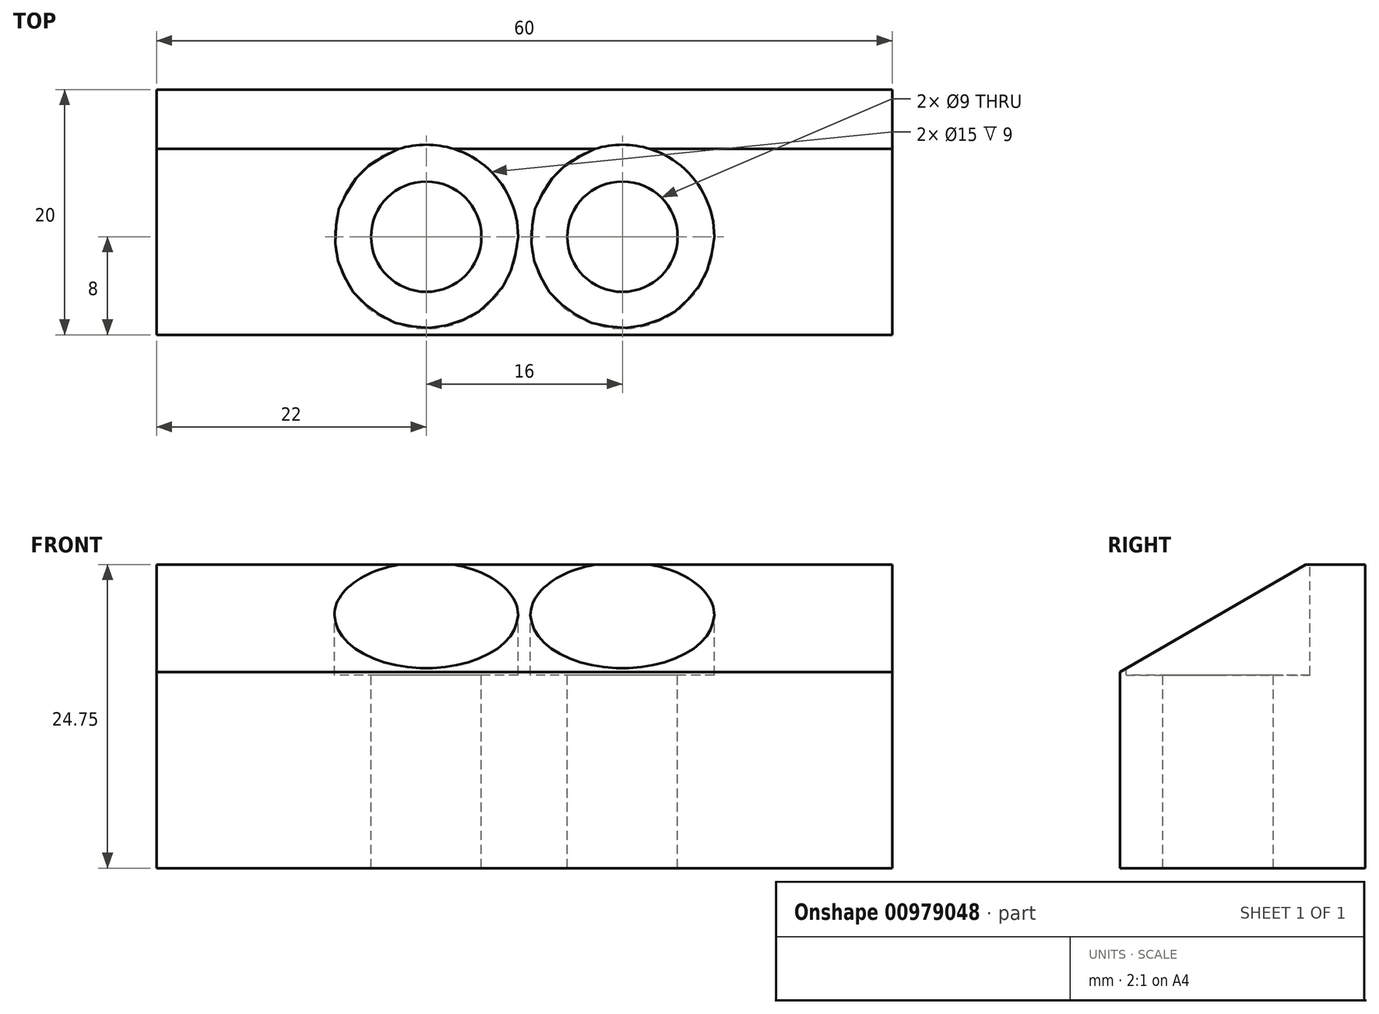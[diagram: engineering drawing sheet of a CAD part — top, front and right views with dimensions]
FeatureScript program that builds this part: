
annotation { "Feature Type Name" : "Feature", "Feature Type Description" : "" }
export const myFeature = defineFeature(function(context is Context, id is Id, definition is map)
    precondition{}
    {
        {
            var Q0;
            Q0=qCreatedBy(makeId("Right.planeOp"),FACE);
            var sketch = newSketch(context, id + "F0", { "sketchPlane" : qUnion([Q0])});
            skLineSegment(sketch, "E0", {"start": v(0, 0) * mm, "end": v(0, 24.75) * mm});
            skLineSegment(sketch, "E1", {"start": v(0, 24.75) * mm, "end": v(-4.84, 24.75) * mm});
            skLineSegment(sketch, "E2", {"start": v(-4.84, 24.75) * mm, "end": v(-20, 16) * mm});
            skLineSegment(sketch, "E3", {"start": v(-20, 16) * mm, "end": v(-20, 0) * mm});
            skLineSegment(sketch, "E4", {"start": v(-20, 0) * mm, "end": v(0, 0) * mm});
            skSolve(sketch);
        }
        {
            var Q0;
            Q0=makeQuery(id+"F0.imprint","IMPRINT",FACE,{"disambiguationData":[TD([[makeQuery(id+"F0.imprint","IMPRINT",EDGE,{"derivedFrom":sQuery(id+"F0.wireOp",EDGE,"E0")}),1.0]])]});
            extrude(context, id + "F1", {"entities" : qUnion([Q0]), "endBound" : BoundingType.SYMMETRIC, "depth" : 60 * mm, "offsetDistance" : 25 * mm});
        }
        {
            var Q0;
            Q0=makeQuery(id+"F1.opExtrude","SWEPT_FACE",FACE,{"disambiguationData":[OSD([sQuery(id+"F0.wireOp",EDGE,"E1")])]});
            var sketch = newSketch(context, id + "F2", { "sketchPlane" : qUnion([Q0])});
            skPoint(sketch, "E5", {"position": v(8, -12) * mm});
            skPoint(sketch, "E6", {"position": v(-8, -12) * mm});
            skSolve(sketch);
        }
        {
            var Q0;
            Q0=sQuery(id+"F2.wireOp",VERTEX,"E6");
            var Q1;
            Q1=sQuery(id+"F2.wireOp",VERTEX,"E5");
            var Q2;
            Q2=makeQuery(id+"F1.opExtrude","SWEPT_BODY",BODY,{"disambiguationData":[OSD([sQuery(id+"F0.wireOp",EDGE,"E0"),sQuery(id+"F0.wireOp",EDGE,"E1"),sQuery(id+"F0.wireOp",EDGE,"E2"),sQuery(id+"F0.wireOp",EDGE,"E3"),sQuery(id+"F0.wireOp",EDGE,"E4")])]});
            hole(context, id + "F3", {"style" : HoleStyle.C_BORE, "endStyle" : HoleEndStyle.THROUGH, "holeDiameter" : 9 * mm, "cBoreDiameter" : 15 * mm, "cBoreDepth" : 9 * mm, "majorDiameter" : 8 * mm, "isTappedThrough" : true, "tappedDepth" : 12 * mm, "tapClearance" : 3, "startFromSketch" : true, "locations" : qUnion([Q0, Q1]), "scope" : qUnion([Q2])});
        }
    });
